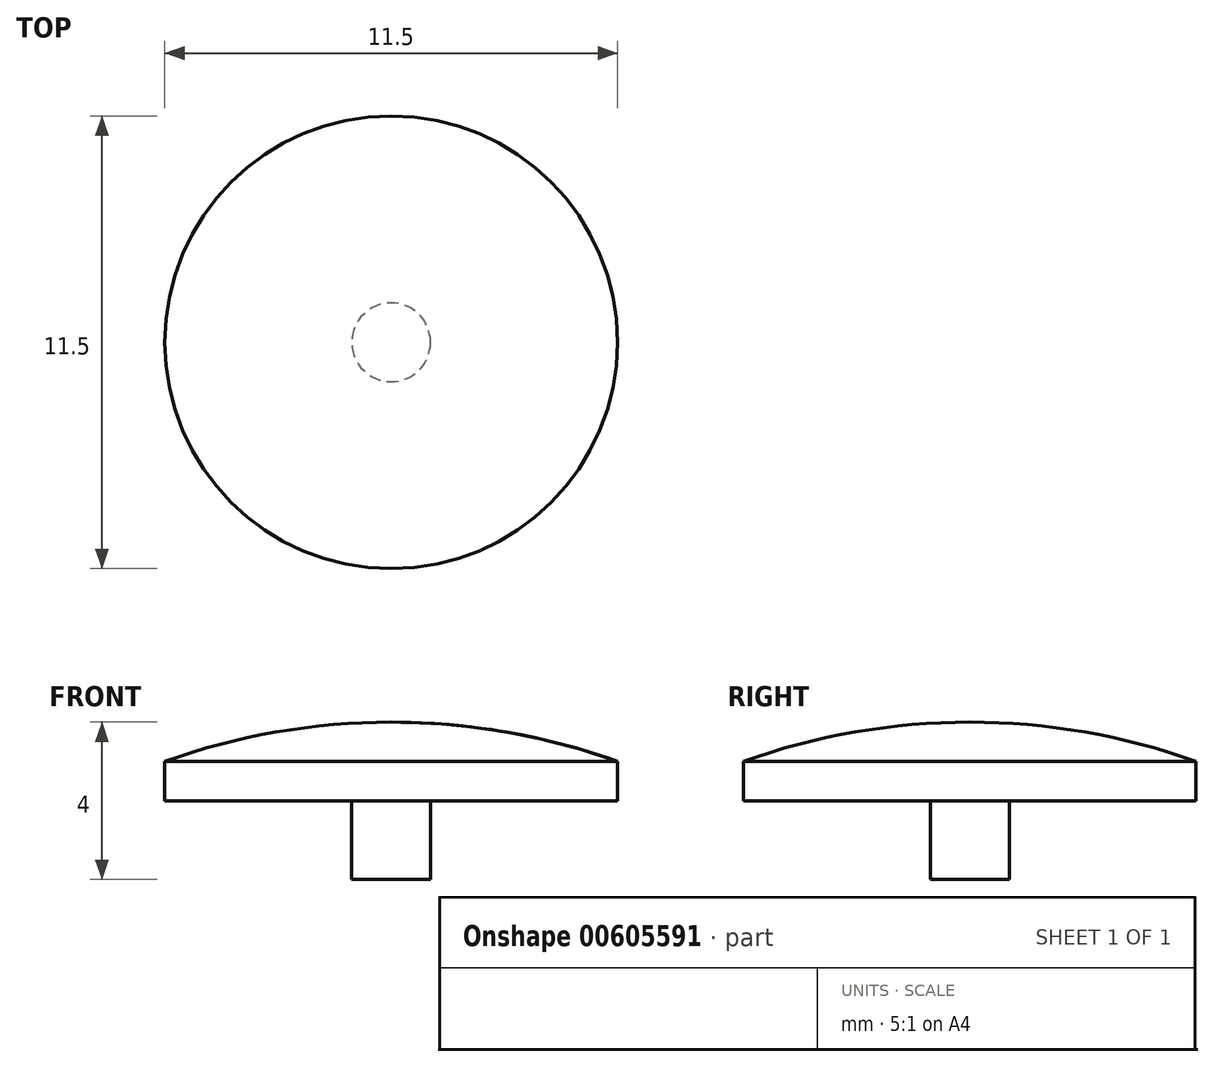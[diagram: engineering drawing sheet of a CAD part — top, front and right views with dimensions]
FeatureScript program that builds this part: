
annotation { "Feature Type Name" : "Feature", "Feature Type Description" : "" }
export const myFeature = defineFeature(function(context is Context, id is Id, definition is map)
    precondition{}
    {
        {
            var Q0;
            Q0=qCreatedBy(makeId("Front.planeOp"),FACE);
            var sketch = newSketch(context, id + "F0", { "sketchPlane" : qUnion([Q0])});
            skLineSegment(sketch, "E0", {"start": v(0, 9.97) * mm, "end": v(0, -9.97) * mm, "construction": true});
            skLineSegment(sketch, "E1", {"start": v(0, 2) * mm, "end": v(-5.75, 2) * mm, "construction": true});
            skLineSegment(sketch, "E2", {"start": v(-5.75, 2) * mm, "end": v(-5.75, 1) * mm, "construction": true});
            skLineSegment(sketch, "E3", {"start": v(-5.75, 1) * mm, "end": v(-5.75, 0) * mm});
            skLineSegment(sketch, "E4", {"start": v(1, 0) * mm, "end": v(1, -2) * mm});
            skLineSegment(sketch, "E5", {"start": v(0, -2) * mm, "end": v(1, -2) * mm});
            skLineSegment(sketch, "E6.MirrorCS", {"start": v(0, 2) * mm, "end": v(5.75, 2) * mm, "construction": true});
            skLineSegment(sketch, "E7.MirrorCS", {"start": v(5.75, 2) * mm, "end": v(5.75, 1) * mm, "construction": true});
            skLineSegment(sketch, "E8.MirrorCS", {"start": v(5.75, 1) * mm, "end": v(5.75, 0) * mm});
            skLineSegment(sketch, "E9.MirrorCS", {"start": v(0, -2) * mm, "end": v(-1, -2) * mm});
            skLineSegment(sketch, "E10.MirrorCS", {"start": v(-1, 0) * mm, "end": v(-1, -2) * mm});
            skArc(sketch, "E11", {"start": v(5.75, 1) * mm, "mid": v(0, 2) * mm, "end": v(-5.75, 1) * mm});
            skLineSegment(sketch, "E12", {"start": v(-5.75, 0) * mm, "end": v(-1, 0) * mm});
            skLineSegment(sketch, "E13", {"start": v(1, 0) * mm, "end": v(5.75, 0) * mm});
            skLineSegment(sketch, "E14", {"start": v(0, 2) * mm, "end": v(0, -2) * mm});
            skSolve(sketch);
        }
        {
            var Q0;
            Q0=makeQuery(id+"F0.imprint","IMPRINT",FACE,{"disambiguationData":[TD([[makeQuery(id+"F0.imprint","IMPRINT",EDGE,{"derivedFrom":sQuery(id+"F0.wireOp",EDGE,"E3")}),1.0]])]});
            var Q1;
            Q1=sQuery(id+"F0.wireOp",EDGE,"E0");
            revolve(context, id + "F1", {"entities" : qUnion([Q0]), "axis" : qUnion([Q1]), "revolveType" : RevolveType.FULL});
        }
    });
